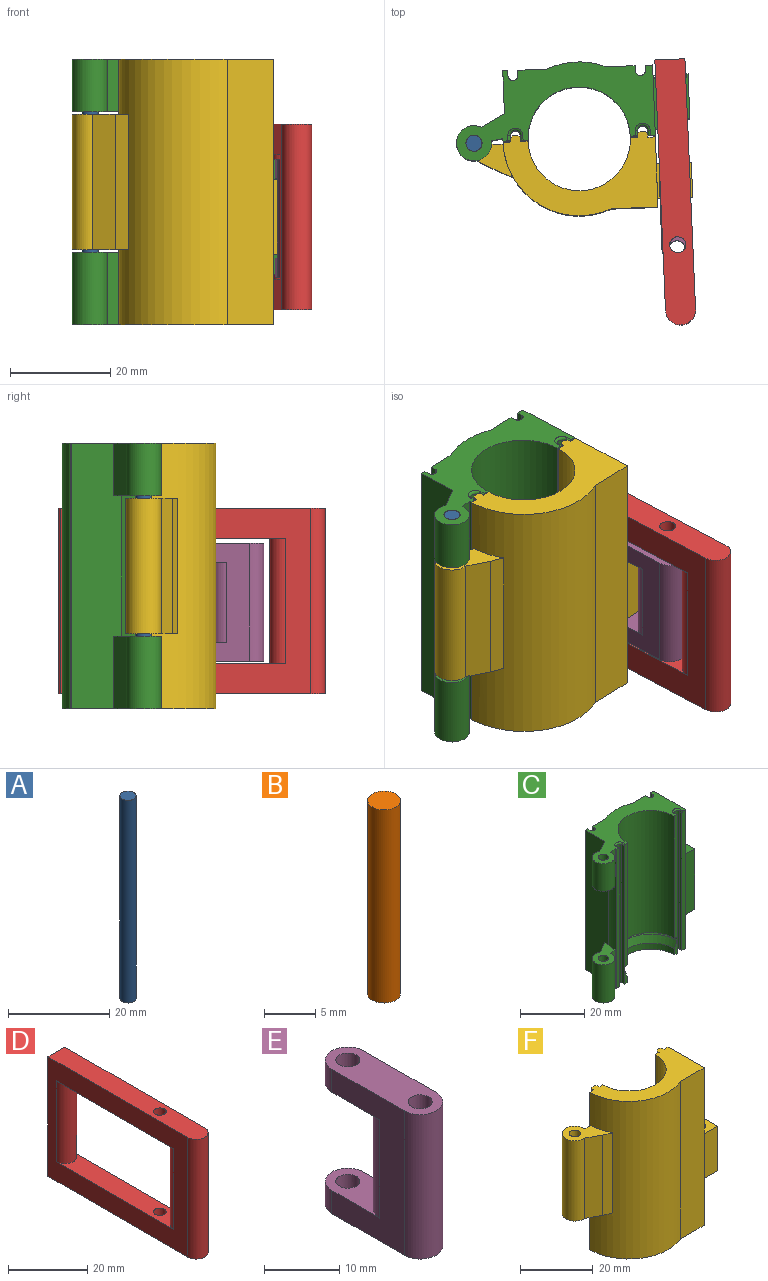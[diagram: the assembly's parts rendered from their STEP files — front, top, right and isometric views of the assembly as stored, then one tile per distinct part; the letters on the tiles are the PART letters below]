
ASSEMBLY  parts=6 mates=5
PART A: 3 faces, bbox 3.2x3.2x49 mm
  f0: cylinder r=1.6mm len=49mm, axis (0,0,-1), area 492.6mm2, adj f1,f2
  f1: plane 3.2x3.2mm, normal (0,0,1), area 8mm2, adj f0
  f2: plane 3.2x3.2mm, normal (0,0,-1), area 8mm2, adj f0
PART B: 3 faces, bbox 3.2x3.2x23 mm
  f0: cylinder r=1.6mm len=23mm, axis (0,0,1), area 231.2mm2, adj f1,f2
  f1: plane 3.2x3.2mm, normal (0,0,-1), area 8mm2, adj f0
  f2: plane 3.2x3.2mm, normal (0,0,1), area 8mm2, adj f0
PART C: 57 faces, bbox 46.7x18.9x53 mm
  f0: cylinder r=15.2mm len=53mm, axis (0,0,1), area 644.5mm2, adj f7,f8,f51,f53
  f1: plane 23x0.25mm, normal (0,1,0), area 5.8mm2, adj f2,f40,f42,f45
  f2: plane 53x14mm, normal (1,0,0), area 489mm2, adj f1,f4,f7,f8,f40,f42,f46,f49
  f3: plane 5.6x1.25mm, normal (0,-1,0), area 4.9mm2, adj f7,f10,f11,f17,f56
  f4: plane 53x1.5mm, normal (0,-1,0), area 79.4mm2, adj f2,f7,f8,f18,f24
  f5: plane 53x1.5mm, normal (0,-1,0), area 79.4mm2, adj f7,f8,f9,f21,f27
  f6: plane 5.6x1.25mm, normal (0,-1,0), area 4.9mm2, adj f7,f10,f11,f19,f56
  f7: plane 39.7x18.9mm, normal (0,0,-1), area 288mm2, adj f0,f2,f3,f4,f5,f6,f9,f10
  f8: plane 39.7x18.9mm, normal (0,0,1), area 290.1mm2, adj f0,f2,f4,f5,f9,f13,f14,f15
  f9: cylinder r=15.2mm len=53mm, axis (0,0,1), area 121.6mm2, adj f5,f7,f8,f31,f33,f35,f37,f47
  f10: cylinder r=10.45mm len=20.9mm, axis (0,0,1), area 76.3mm2, adj f3,f6,f7,f56
  f11: torus R=10.8mm, axis (0,0,1), area 74.5mm2, adj f3,f6,f12,f14,f15,f56
  f12: plane 21.6x10.8mm, normal (0,0,-1), area 19.8mm2, adj f11,f13,f14,f15
  f13: cylinder r=10.2mm len=46.5mm, axis (0,0,1), area 1490.1mm2, adj f8,f12,f14,f15
  f14: plane 47.4x1.5mm, normal (0,-1,0), area 69.9mm2, adj f8,f11,f12,f13,f17,f26
  f15: plane 47.4x1.5mm, normal (0,-1,0), area 69.9mm2, adj f8,f11,f12,f13,f19,f29
  f16: cylinder r=1mm len=52.5mm, axis (0,0,1), area 164.9mm2, adj f7,f17,f18,f25
  f17: plane 52.5x1mm, normal (1,0,0), area 52.5mm2, adj f3,f7,f14,f16,f26
  f18: plane 52.5x1mm, normal (-1,0,0), area 52.5mm2, adj f4,f7,f16,f24
  f19: plane 52.5x1mm, normal (-1,0,0), area 52.5mm2, adj f6,f7,f15,f20,f29
  f20: cylinder r=1mm len=52.5mm, axis (0,0,1), area 164.9mm2, adj f7,f19,f21,f28
  f21: plane 52.5x1mm, normal (1,0,0), area 52.5mm2, adj f5,f7,f20,f27
  f22: cylinder r=1mm len=53mm, axis (0,0,1), area 166.5mm2, adj f7,f8,f52,f54
  f23: cylinder r=1mm len=53mm, axis (0,0,1), area 166.5mm2, adj f7,f8,f48,f50
  f24: cylinder r=0.5mm len=1mm, axis (0,-1,0), area 0.8mm2, adj f4,f8,f18,f25
  f25: torus R=1.5mm, axis (0,0,1), area 2.9mm2, adj f8,f16,f24,f26
  f26: cylinder r=0.5mm len=1mm, axis (0,1,0), area 0.8mm2, adj f8,f14,f17,f25
  f27: cylinder r=0.5mm len=1mm, axis (0,1,0), area 0.8mm2, adj f5,f8,f21,f28
  f28: torus R=1.5mm, axis (0,0,1), area 2.9mm2, adj f8,f20,f27,f29
  f29: cylinder r=0.5mm len=1mm, axis (0,-1,0), area 0.8mm2, adj f8,f15,f19,f28
  f30: cylinder r=3.5mm len=14.5mm, axis (0,0,-1), area 268.1mm2, adj f7,f31,f32,f33
  f31: plane 9.8x9.19mm, normal (0,0,1), area 44.3mm2, adj f9,f30,f32,f33,f39,f47
  f32: plane 14.5x4.71mm, normal (-0.48,0.88,0), area 77.8mm2, adj f7,f30,f31,f47
  f33: plane 14.5x2.32mm, normal (0.14,-0.99,0), area 34mm2, adj f7,f9,f30,f31
  f34: cylinder r=3.5mm len=10.5mm, axis (0,0,-1), area 194.2mm2, adj f8,f35,f36,f37
  f35: plane 9.8x9.19mm, normal (0,0,-1), area 44.3mm2, adj f9,f34,f36,f37,f38,f47
  f36: plane 10.5x4.71mm, normal (-0.48,0.88,0), area 56.3mm2, adj f8,f34,f35,f47
  f37: plane 10.5x2.32mm, normal (0.14,-0.99,0), area 24.7mm2, adj f8,f9,f34,f35
  f38: cylinder r=1.6mm len=10.5mm, axis (0,0,1), area 105.6mm2, adj f8,f35
  f39: cylinder r=1.6mm len=14.5mm, axis (0,0,1), area 145.8mm2, adj f7,f31
  f40: plane 11x7mm, normal (0,0,1), area 48.4mm2, adj f1,f2,f41,f43,f44,f45,f46
  f41: plane 23x5mm, normal (0,-1,0), area 115mm2, adj f40,f42,f44,f46
  f42: plane 11x7mm, normal (0,0,-1), area 48.4mm2, adj f1,f2,f41,f43,f44,f45,f46
  f43: plane 23x0.25mm, normal (0,1,0), area 5.8mm2, adj f40,f42,f44,f45
  f44: plane 23x9mm, normal (1,0,0), area 207mm2, adj f40,f41,f42,f43
  f45: cylinder r=3.25mm len=23mm, axis (0,0,1), area 234.8mm2, adj f1,f40,f42,f43
  f46: plane 23x2mm, normal (0.71,-0.71,0), area 65.1mm2, adj f2,f40,f41,f42
  f47: plane 53x10.13mm, normal (-1,0,0), area 496.5mm2, adj f7,f8,f9,f31,f32,f35,f36,f55
  f48: plane 53x1mm, normal (-1,0,0), area 53mm2, adj f7,f8,f23,f49
  f49: plane 53x1.5mm, normal (0,1,0), area 79.5mm2, adj f2,f7,f8,f48
  f50: plane 53x1mm, normal (1,0,0), area 53mm2, adj f7,f8,f23,f51
  f51: plane 53x5.78mm, normal (0,1,0), area 306.4mm2, adj f0,f7,f8,f50
  f52: plane 53x1mm, normal (-1,0,0), area 53mm2, adj f7,f8,f22,f53
  f53: plane 53x5.78mm, normal (0,1,0), area 306.4mm2, adj f0,f7,f8,f52
  f54: plane 53x1mm, normal (1,0,0), area 53mm2, adj f7,f8,f22,f55
  f55: plane 53x1mm, normal (0,1,0), area 53mm2, adj f7,f8,f47,f54
  f56: cone r=10.2mm half-angle=20.9deg, axis (0,0,1), area 98.6mm2, adj f3,f6,f10,f11
PART D: 12 faces, bbox 6x53x37 mm
  f0: plane 53x6mm, normal (0,0,-1), area 306.1mm2, adj f1,f5,f6,f10,f11
  f1: plane 37x6mm, normal (0,1,0), area 222mm2, adj f0,f2,f5,f6
  f2: plane 53x6mm, normal (0,0,1), area 306.1mm2, adj f1,f5,f6,f9,f11
  f3: plane 42x6mm, normal (0,0,1), area 215.7mm2, adj f5,f6,f7,f8,f10
  f4: plane 42x6mm, normal (0,0,-1), area 215.7mm2, adj f5,f6,f7,f8,f9
  f5: plane 50x37mm, normal (1,0,0), area 800mm2, adj f0,f1,f2,f3,f4,f7,f8,f11
  f6: plane 50x37mm, normal (-1,0,0), area 800mm2, adj f0,f1,f2,f3,f4,f7,f8,f11
  f7: cylinder r=3mm len=25mm, axis (0,0,-1), area 235.6mm2, adj f3,f4,f5,f6
  f8: cylinder r=3mm len=25mm, axis (0,0,1), area 235.6mm2, adj f3,f4,f5,f6
  f9: cylinder r=1.6mm len=6mm, axis (0,0,1), area 60.3mm2, adj f2,f4
  f10: cylinder r=1.6mm len=6mm, axis (0,0,1), area 60.3mm2, adj f0,f3
  f11: cylinder r=3mm len=37mm, axis (0,0,-1), area 348.7mm2, adj f0,f2,f5,f6
PART E: 13 faces, bbox 6x19.6x23.5 mm
  f0: plane 12x6mm, normal (0,0,-1), area 46mm2, adj f4,f5,f7,f9,f12
  f1: plane 19.6x6mm, normal (0,0,1), area 93.8mm2, adj f4,f5,f7,f8,f10,f12
  f2: plane 19.6x6mm, normal (0,0,-1), area 93.8mm2, adj f4,f5,f6,f8,f10,f11
  f3: plane 12x6mm, normal (0,0,1), area 46mm2, adj f4,f5,f6,f9,f11
  f4: plane 23.5x13.6mm, normal (1,0,0), area 175.6mm2, adj f0,f1,f2,f3,f9,f10,f11,f12
  f5: plane 23.5x13.6mm, normal (-1,0,0), area 175.6mm2, adj f0,f1,f2,f3,f9,f10,f11,f12
  f6: cylinder r=1.6mm len=3.75mm, axis (0,0,1), area 37.7mm2, adj f2,f3
  f7: cylinder r=1.6mm len=3.75mm, axis (0,0,1), area 37.7mm2, adj f0,f1
  f8: cylinder r=1.6mm len=23.5mm, axis (0,0,1), area 236.2mm2, adj f1,f2
  f9: cylinder r=3mm len=16mm, axis (0,0,-1), area 150.8mm2, adj f0,f3,f4,f5
  f10: cylinder r=3mm len=23.5mm, axis (0,0,1), area 221.5mm2, adj f1,f2,f4,f5
  f11: cylinder r=3mm len=6mm, axis (0,0,-1), area 35.3mm2, adj f2,f3,f4,f5
  f12: cylinder r=3mm len=6mm, axis (0,0,-1), area 35.3mm2, adj f0,f1,f4,f5
PART F: 40 faces, bbox 46.7x18.7x53 mm
  f0: cylinder r=15.2mm len=53mm, axis (0,0,-1), area 1400.1mm2, adj f3,f8,f13,f27,f29,f30,f31,f38
  f1: plane 5.6x1.25mm, normal (0,1,0), area 4.7mm2, adj f5,f9,f21,f38,f39
  f2: plane 53x1.5mm, normal (0,1,0), area 79.5mm2, adj f8,f12,f19,f38
  f3: plane 53x1.5mm, normal (0,1,0), area 79.5mm2, adj f0,f8,f16,f38
  f4: plane 5.6x1.25mm, normal (0,1,0), area 4.7mm2, adj f5,f9,f14,f38,f39
  f5: torus R=10.8mm, axis (0,0,-1), area 72.3mm2, adj f1,f4,f6,f10,f11,f39
  f6: plane 21.6x10.8mm, normal (0,0,-1), area 19.8mm2, adj f5,f7,f10,f11
  f7: cylinder r=10.2mm len=46.5mm, axis (0,0,-1), area 1490.1mm2, adj f6,f8,f10,f11
  f8: plane 30.4x16.4mm, normal (0,0,1), area 239.9mm2, adj f0,f2,f3,f7,f10,f11,f12,f13
  f9: cylinder r=10.45mm len=20.9mm, axis (0,0,-1), area 64.6mm2, adj f1,f4,f38,f39
  f10: plane 47.4x1.5mm, normal (0,1,0), area 69.9mm2, adj f5,f6,f7,f8,f21
  f11: plane 47.4x1.5mm, normal (0,1,0), area 69.9mm2, adj f5,f6,f7,f8,f14
  f12: plane 53x14mm, normal (1,0,0), area 637mm2, adj f2,f8,f13,f32,f33,f34,f35,f38
  f13: plane 53x9.28mm, normal (0,-1,0), area 491.9mm2, adj f0,f8,f12,f38
  f14: plane 53x0.7mm, normal (1,0,0), area 37.1mm2, adj f4,f8,f11,f18,f38
  f15: plane 53x1mm, normal (0,1,0), area 53mm2, adj f8,f17,f18,f38
  f16: plane 53x0.7mm, normal (-1,0,0), area 37.1mm2, adj f3,f8,f17,f38
  f17: plane 53x0.5mm, normal (-0.71,0.71,0), area 37.5mm2, adj f8,f15,f16,f38
  f18: plane 53x0.5mm, normal (0.71,0.71,0), area 37.5mm2, adj f8,f14,f15,f38
  f19: plane 53x0.7mm, normal (1,0,0), area 37.1mm2, adj f2,f8,f23,f38
  f20: plane 53x1mm, normal (0,1,0), area 53mm2, adj f8,f22,f23,f38
  f21: plane 53x0.7mm, normal (-1,0,0), area 37.1mm2, adj f1,f8,f10,f22,f38
  f22: plane 53x0.5mm, normal (-0.71,0.71,0), area 37.5mm2, adj f8,f20,f21,f38
  f23: plane 53x0.5mm, normal (0.71,0.71,0), area 37.5mm2, adj f8,f19,f20,f38
  f24: plane 27x0.38mm, normal (0.17,0.99,0), area 10.3mm2, adj f25,f29,f30,f31
  f25: cylinder r=3.5mm len=27mm, axis (0,0,-1), area 463.2mm2, adj f24,f26,f30,f31
  f26: plane 27x4.48mm, normal (-0.47,-0.88,0), area 137.3mm2, adj f25,f27,f30,f31
  f27: plane 27x2.7mm, normal (-0.39,-0.92,0), area 79.3mm2, adj f0,f26,f30,f31
  f28: cylinder r=1.6mm len=27mm, axis (0,0,-1), area 271.4mm2, adj f30,f31
  f29: plane 27x1.94mm, normal (0,1,0), area 52.4mm2, adj f0,f24,f30,f31
  f30: plane 11.03x10.54mm, normal (0,0,1), area 51.4mm2, adj f0,f24,f25,f26,f27,f28,f29
  f31: plane 11.03x10.54mm, normal (0,0,-1), area 51.4mm2, adj f0,f24,f25,f26,f27,f28,f29
  f32: plane 7x7mm, normal (0,0,1), area 41mm2, adj f12,f33,f35,f36,f37
  f33: plane 15x7mm, normal (0,-1,0), area 105mm2, adj f12,f32,f34,f36
  f34: plane 7x7mm, normal (0,0,-1), area 41mm2, adj f12,f33,f35,f36,f37
  f35: plane 15x7mm, normal (0,1,0), area 105mm2, adj f12,f32,f34,f36
  f36: plane 15x7mm, normal (1,0,0), area 105mm2, adj f32,f33,f34,f35
  f37: cylinder r=1.6mm len=15mm, axis (0,0,-1), area 150.8mm2, adj f32,f34
  f38: plane 30.4x16.4mm, normal (0,0,-1), area 231.8mm2, adj f0,f1,f2,f3,f4,f9,f12,f13
  f39: cone r=11.51mm half-angle=19deg, axis (0,0,1), area 112.3mm2, adj f1,f4,f5,f9
PLACE A t=(128.94,-47.81,-22.02)mm
PLACE B rot(axis=(0,0,1),2deg) t=(145.17,-62.12,-4.77)mm
PLACE C rot(axis=(0,0,1),2.2deg) t=(128.92,-46.79,-22.02)mm
PLACE D rot(axis=(0,0,1),2.4deg) t=(145.03,-55.17,-4.52)mm
PLACE E rot(axis=(0,0,1),2deg) t=(145.17,-62.12,-4.77)mm
PLACE F rot(axis=(0,0,1),2deg) t=(128.93,-47.08,-22.02)mm
MATE revolute B.f0 <-> F.f37  axis (0,0,1) through (147.93,-55.22,-4.52)mm
MATE revolute D.f8 <-> C.f45  axis (0,0,1) through (147.13,-34.06,-4.52)mm
MATE revolute E.f11 <-> B.f0  axis (0,0,1) through (147.93,-55.22,6.98)mm
MATE revolute A.f0 <-> C.f30  axis (0,0,1) through (107.94,-47.81,26.98)mm
MATE revolute A.f0 <-> F.f25  axis (0,0,-1) through (107.94,-47.81,2.48)mm
